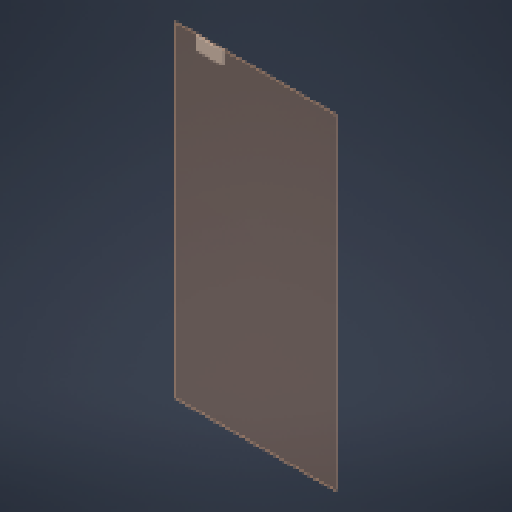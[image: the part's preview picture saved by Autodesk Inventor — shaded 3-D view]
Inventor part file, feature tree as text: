
AUTODESK INVENTOR PART (.ipt)
format: ipt  version: 2024 (Build 280153000, 153)  size: 125,440 bytes
history: native  units: mm
features: other x5, plane x1, extrude x1, sketch x1
ambient origin geometry x8: Origin, YZ Plane, XZ Plane, XY Plane, X Axis, Y Axis, Z Axis, Center Point
bodies: Body1 (feature_tree)
feature tree (8):
  other  "Sólido1"
  plane  "Plano de trabajo1"
  extrude  "Extrusión1"  Depth=30.0mm
  sketch  "Boceto1"  dims[d0=120.0mm d1=30.0mm d2=30.0mm d3=30.0mm d4=2.0mm d5=0.0mm]
  other  "<userpath>\Downloads\Piezas CMR\Marco_APM_002\Marco_apm_002-4.iam"
  other  "Marco_apm_002-4.iam"
  other  "Marco_Conveyor_Aereo:1"
  other  "Marco:1"
